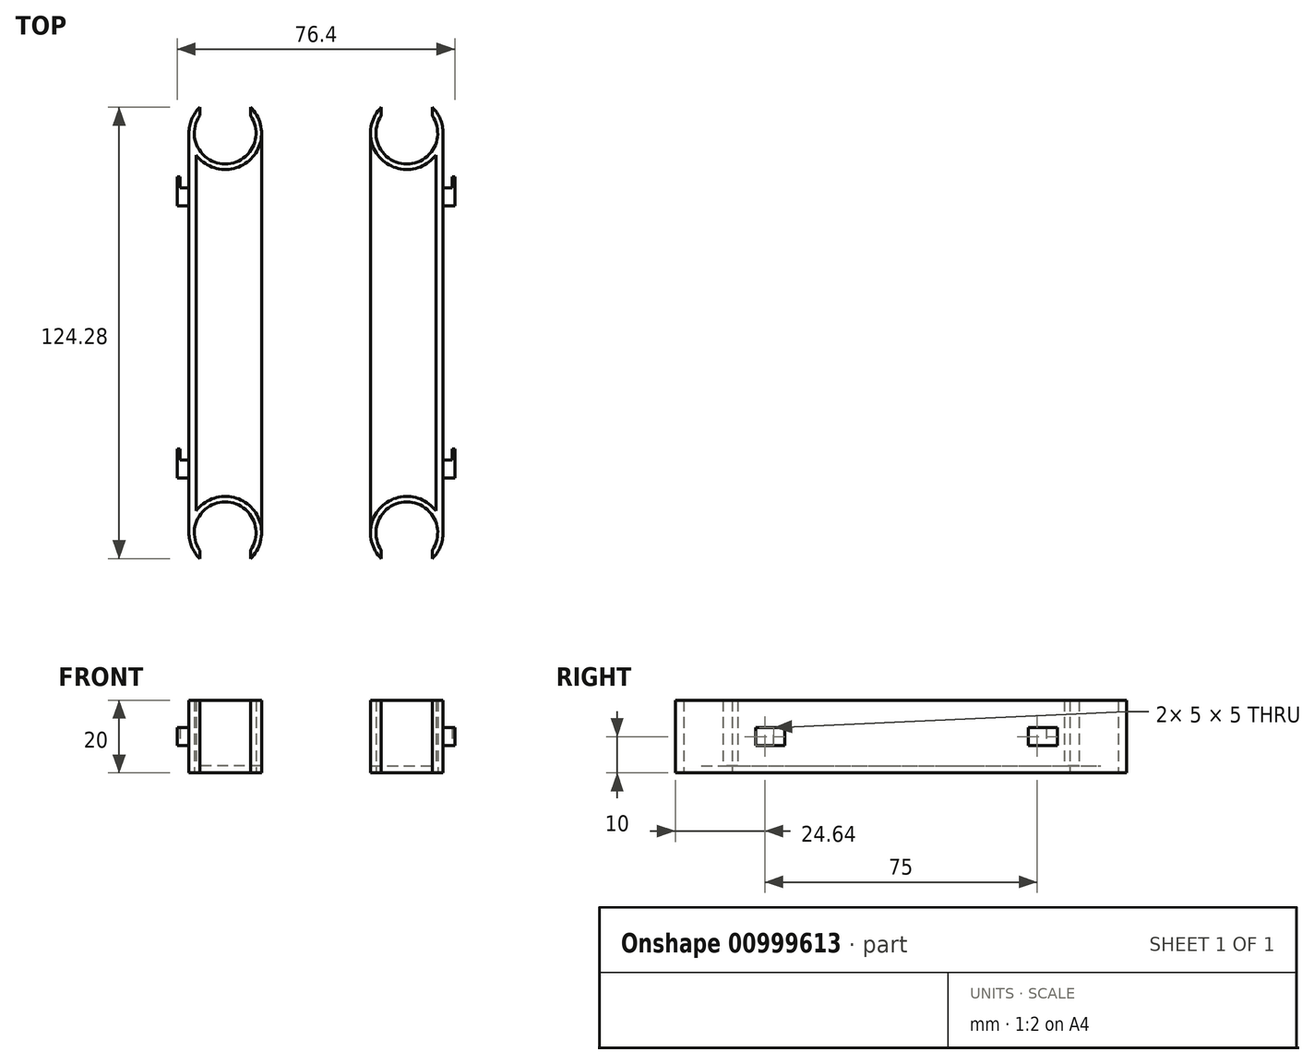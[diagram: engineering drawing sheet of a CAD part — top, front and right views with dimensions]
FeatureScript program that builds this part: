
annotation { "Feature Type Name" : "Feature", "Feature Type Description" : "" }
export const myFeature = defineFeature(function(context is Context, id is Id, definition is map)
    precondition{}
    {
        {
            var Q0;
            Q0=qCreatedBy(makeId("Top.planeOp"),FACE);
            var sketch = newSketch(context, id + "F0", { "sketchPlane" : qUnion([Q0])});
            skCircle(sketch, "E0", {"center": v(0, 0) * mm, "radius": 10 * mm});
            skLineSegment(sketch, "E1", {"start": v(-10, 0) * mm, "end": v(-10, 110) * mm});
            skLineSegment(sketch, "E2", {"start": v(0, 0) * mm, "end": v(0, 110) * mm, "construction": true});
            skCircle(sketch, "E3", {"center": v(0, 110) * mm, "radius": 10 * mm});
            skLineSegment(sketch, "E4", {"start": v(-8, 6) * mm, "end": v(-8, 104) * mm});
            skLineSegment(sketch, "E5", {"start": v(10, 0) * mm, "end": v(10, 110) * mm});
            skCircle(sketch, "E6", {"center": v(0, 0) * mm, "radius": 8.5 * mm});
            skCircle(sketch, "E7", {"center": v(0, 110) * mm, "radius": 8.5 * mm});
            skLineSegment(sketch, "E8", {"start": v(-10, 55) * mm, "end": v(10, 55) * mm, "construction": true});
            skLineSegment(sketch, "E9", {"start": v(0, 0) * mm, "end": v(0, -10) * mm, "construction": true});
            skLineSegment(sketch, "E10", {"start": v(0, 10) * mm, "end": v(0, 0) * mm, "construction": true});
            skPoint(sketch, "E11", {"position": v(0, 101.5) * mm});
            skPoint(sketch, "E12", {"position": v(0, 8.5) * mm});
            skLineSegment(sketch, "E13", {"start": v(-10, 0) * mm, "end": v(10, 0) * mm, "construction": true});
            skLineSegment(sketch, "E14", {"start": v(-10, 110) * mm, "end": v(10, 110) * mm, "construction": true});
            skLineSegment(sketch, "E15", {"start": v(7, 0) * mm, "end": v(7, -12.96) * mm});
            skLineSegment(sketch, "E16", {"start": v(-7, 0) * mm, "end": v(-7, -12.96) * mm});
            skLineSegment(sketch, "E17.MirrorCS", {"start": v(-7, 110) * mm, "end": v(-7, 122.96) * mm});
            skLineSegment(sketch, "E18.MirrorCS", {"start": v(7, 110) * mm, "end": v(7, 122.96) * mm});
            skSolve(sketch);
        }
        {
            var Q0;
            {var subQ0=sQuery(id+"F0.wireOp",EDGE,"E1");Q0=makeQuery(id+"F0.imprint","IMPRINT",FACE,{"disambiguationData":[TD([[makeQuery(id+"F0.imprint","IMPRINT",EDGE,{"derivedFrom":subQ0}),-1.0]])]});}
            var Q1;
            {var subQ0=sQuery(id+"F0.wireOp",EDGE,"E3");var subQ4=makeQuery(id+"F0.imprint","INTERSECT",VERTEX,{"derivedFrom":[sQuery(id+"F0.wireOp",EDGE,"E1"),subQ0]});Q1=makeQuery(id+"F0.imprint","IMPRINT",FACE,{"disambiguationData":[TD([[makeQuery(id+"F0.imprint","IMPRINT",EDGE,{"disambiguationData":[TD([[subQ4,1.0]])],"derivedFrom":subQ0}),1.0]])]});}
            var Q2;
            {var subQ5=sQuery(id+"F0.wireOp",EDGE,"E0");var subQ8=makeQuery(id+"F0.imprint","INTERSECT",VERTEX,{"derivedFrom":[subQ5,sQuery(id+"F0.wireOp",EDGE,"E4")]});Q2=makeQuery(id+"F0.imprint","IMPRINT",FACE,{"disambiguationData":[TD([[makeQuery(id+"F0.imprint","IMPRINT",EDGE,{"disambiguationData":[TD([[subQ8,1.0]])],"derivedFrom":subQ5}),1.0]])]});}
            extrude(context, id + "F1", {"entities" : qUnion([Q0, Q1, Q2]), "depth" : 20 * mm, "offsetDistance" : 25 * mm});
        }
        {
            var Q0;
            {var subQ0=sQuery(id+"F0.wireOp",EDGE,"E4");Q0=makeQuery(id+"F0.imprint","IMPRINT",FACE,{"disambiguationData":[TD([[makeQuery(id+"F0.imprint","IMPRINT",EDGE,{"derivedFrom":subQ0}),-1.0]])]});}
            extrude(context, id + "F2", {"entities" : qUnion([Q0]), "operationType" : NewBodyOperationType.ADD, "depth" : 2 * mm, "offsetDistance" : 25 * mm});
        }
        {
            var Q0;
            Q0=makeQuery(id+"F1.opExtrude","SWEPT_FACE",FACE,{"disambiguationData":[OSD([sQuery(id+"F0.wireOp",EDGE,"E1")])]});
            var sketch = newSketch(context, id + "F3", { "sketchPlane" : qUnion([Q0])});
            skLineSegment(sketch, "E19.bottom", {"start": v(-95, 12.5) * mm, "end": v(-15, 12.5) * mm});
            skLineSegment(sketch, "E19.top", {"start": v(-95, 7.5) * mm, "end": v(-15, 7.5) * mm});
            skLineSegment(sketch, "E19.left", {"start": v(-95, 12.5) * mm, "end": v(-95, 7.5) * mm});
            skLineSegment(sketch, "E19.right", {"start": v(-15, 12.5) * mm, "end": v(-15, 7.5) * mm});
            skPoint(sketch, "E19.middle", {"position": v(-55, 10) * mm});
            skPoint(sketch, "E19.middle.positionSnap0", {"position": v(0, 10) * mm});
            skPoint(sketch, "E19.middle.positionSnap1", {"position": v(-55, 0) * mm});
            skPoint(sketch, "E19.centerSnap0", {"position": v(0, 10) * mm});
            skPoint(sketch, "E19.centerSnap1", {"position": v(-55, 0) * mm});
            skLineSegment(sketch, "E20", {"start": v(-90, 7.5) * mm, "end": v(-90, 12.5) * mm});
            skLineSegment(sketch, "E21", {"start": v(-20, 7.5) * mm, "end": v(-20, 12.5) * mm});
            skLineSegment(sketch, "E22", {"start": v(-95, 7.5) * mm, "end": v(-98, 7.5) * mm});
            skLineSegment(sketch, "E23", {"start": v(-98, 7.5) * mm, "end": v(-98, 12.5) * mm});
            skLineSegment(sketch, "E24", {"start": v(-98, 12.5) * mm, "end": v(-95, 12.5) * mm});
            skLineSegment(sketch, "E25", {"start": v(-23, 12.5) * mm, "end": v(-23, 7.5) * mm});
            skSolve(sketch);
        }
        {
            var Q0;
            {var subQ0=sQuery(id+"F3.wireOp",EDGE,"E19.left");Q0=makeQuery(id+"F3.imprint","IMPRINT",FACE,{"disambiguationData":[TD([[makeQuery(id+"F3.imprint","IMPRINT",EDGE,{"derivedFrom":subQ0}),1.0]])]});}
            var Q1;
            {var subQ0=sQuery(id+"F3.wireOp",EDGE,"E19.right");Q1=makeQuery(id+"F3.imprint","IMPRINT",FACE,{"disambiguationData":[TD([[makeQuery(id+"F3.imprint","IMPRINT",EDGE,{"derivedFrom":subQ0}),-1.0]])]});}
            var Q2;
            Q2=makeQuery(id+"F3.imprint","IMPRINT",FACE,{"disambiguationData":[TD([[makeQuery(id+"F3.imprint","IMPRINT",EDGE,{"derivedFrom":sQuery(id+"F3.wireOp",EDGE,"E19.left")}),-1.0]])]});
            var Q3;
            {var subQ0=sQuery(id+"F3.wireOp",EDGE,"E21");Q3=makeQuery(id+"F3.imprint","IMPRINT",FACE,{"disambiguationData":[TD([[makeQuery(id+"F3.imprint","IMPRINT",EDGE,{"derivedFrom":subQ0}),1.0]])]});}
            extrude(context, id + "F4", {"entities" : qUnion([Q0, Q1, Q2, Q3]), "operationType" : NewBodyOperationType.ADD, "depth" : 3.2 * mm, "offsetDistance" : 25 * mm});
        }
        {
            var Q0;
            Q0=makeQuery(id+"F3.imprint","IMPRINT",FACE,{"disambiguationData":[TD([[makeQuery(id+"F3.imprint","IMPRINT",EDGE,{"derivedFrom":sQuery(id+"F3.wireOp",EDGE,"E19.left")}),-1.0]])]});
            var Q1;
            {var subQ0=sQuery(id+"F3.wireOp",EDGE,"E21");Q1=makeQuery(id+"F3.imprint","IMPRINT",FACE,{"disambiguationData":[TD([[makeQuery(id+"F3.imprint","IMPRINT",EDGE,{"derivedFrom":subQ0}),1.0]])]});}
            extrude(context, id + "F5", {"entities" : qUnion([Q0, Q1]), "operationType" : NewBodyOperationType.REMOVE, "depth" : 2.5 * mm, "offsetDistance" : 25 * mm});
        }
        {
            var Q0;
            Q0=qCreatedBy(makeId("Right.planeOp"),FACE);
            cPlane(context, id + "F6", {"entities" : qUnion([Q0]), "cplaneType" : CPlaneType.OFFSET, "offset" : 25 * mm, "width" : 150 * mm, "height" : 150 * mm});
        }
        {
            var Q0;
            Q0=makeQuery(id+"F1.opExtrude","SWEPT_BODY",BODY,{"disambiguationData":[OSD([sQuery(id+"F0.wireOp",EDGE,"E0"),sQuery(id+"F0.wireOp",EDGE,"E1"),sQuery(id+"F0.wireOp",EDGE,"E3"),sQuery(id+"F0.wireOp",EDGE,"E4"),sQuery(id+"F0.wireOp",EDGE,"E6"),sQuery(id+"F0.wireOp",EDGE,"E7"),sQuery(id+"F0.wireOp",EDGE,"E15"),sQuery(id+"F0.wireOp",EDGE,"E16"),sQuery(id+"F0.wireOp",EDGE,"E17.MirrorCS"),sQuery(id+"F0.wireOp",EDGE,"E18.MirrorCS")])]});
            var Q1;
            Q1=qCreatedBy(id+"F6.planeOp",FACE);
            mirror(context, id + "F7", {"entities" : qUnion([Q0]), "mirrorPlane" : qUnion([Q1])});
        }
    });
